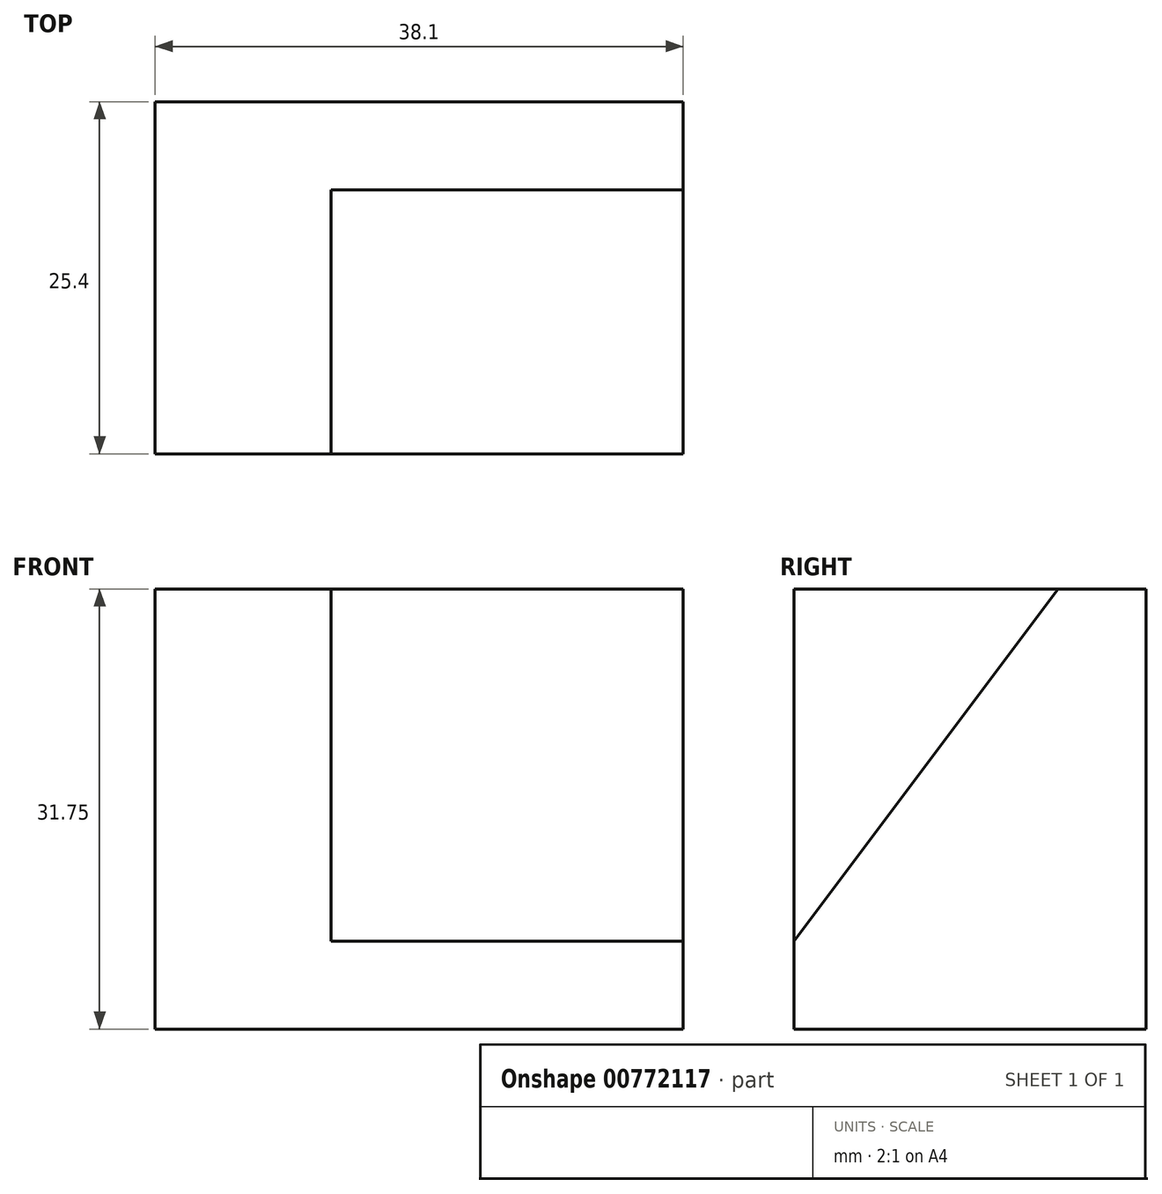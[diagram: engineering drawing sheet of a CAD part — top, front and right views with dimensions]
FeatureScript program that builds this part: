
annotation { "Feature Type Name" : "Feature", "Feature Type Description" : "" }
export const myFeature = defineFeature(function(context is Context, id is Id, definition is map)
    precondition{}
    {
        {
            var Q0;
            Q0=qCreatedBy(makeId("Front.planeOp"),FACE);
            var sketch = newSketch(context, id + "F0", { "sketchPlane" : qUnion([Q0])});
            skLineSegment(sketch, "E0", {"start": v(0, 0) * mm, "end": v(25.4, 0) * mm});
            skLineSegment(sketch, "E1", {"start": v(0, 0) * mm, "end": v(0, 31.75) * mm});
            skLineSegment(sketch, "E2", {"start": v(0, 31.75) * mm, "end": v(25.4, 31.75) * mm});
            skLineSegment(sketch, "E3", {"start": v(25.4, 31.75) * mm, "end": v(25.4, 0) * mm});
            skSolve(sketch);
        }
        {
            var Q0;
            Q0=makeQuery(id+"F0.imprint","IMPRINT",FACE,{"disambiguationData":[TD([[makeQuery(id+"F0.imprint","IMPRINT",EDGE,{"derivedFrom":sQuery(id+"F0.wireOp",EDGE,"E0")}),1.0]])]});
            extrude(context, id + "F1", {"entities" : qUnion([Q0]), "depth" : 25.4 * mm, "offsetDistance" : 25.4 * mm});
        }
        {
            var Q0;
            Q0=makeQuery(id+"F1.opExtrude","SWEPT_FACE",FACE,{"disambiguationData":[OSD([sQuery(id+"F0.wireOp",EDGE,"E3")])]});
            var sketch = newSketch(context, id + "F2", { "sketchPlane" : qUnion([Q0])});
            skLineSegment(sketch, "E4", {"start": v(0, 31.75) * mm, "end": v(-6.35, 31.75) * mm});
            skLineSegment(sketch, "E5", {"start": v(-25.4, 0) * mm, "end": v(-25.4, 6.35) * mm});
            skLineSegment(sketch, "E6", {"start": v(-25.4, 6.35) * mm, "end": v(-6.35, 31.75) * mm});
            skSolve(sketch);
        }
        {
            var Q0;
            Q0=makeQuery(id+"F1.opExtrude","SWEPT_FACE",FACE,{"disambiguationData":[OSD([sQuery(id+"F0.wireOp",EDGE,"E1")])]});
            extrude(context, id + "F3", {"entities" : qUnion([Q0]), "operationType" : NewBodyOperationType.ADD, "depth" : 6.35 * mm, "offsetDistance" : 25.4 * mm});
        }
        {
            var Q0;
            {var subQ0=sQuery(id+"F2.wireOp",EDGE,"E6");Q0=makeQuery(id+"F2.imprint","IMPRINT",FACE,{"disambiguationData":[TD([[makeQuery(id+"F2.imprint","IMPRINT",EDGE,{"derivedFrom":subQ0}),1.0]])]});}
            extrude(context, id + "F4", {"entities" : qUnion([Q0]), "operationType" : NewBodyOperationType.REMOVE, "oppositeDirection" : true, "depth" : 25.4 * mm, "offsetDistance" : 25.4 * mm});
        }
        {
            var Q0;
            Q0=makeQuery(id+"F3.opExtrude","CAP_FACE",FACE,{"disambiguationData":[OSD([sQuery(id+"F0.wireOp",EDGE,"E1")])],"isStart":false});
            extrude(context, id + "F5", {"entities" : qUnion([Q0]), "operationType" : NewBodyOperationType.ADD, "depth" : 6.35 * mm, "offsetDistance" : 25.4 * mm});
        }
    });
